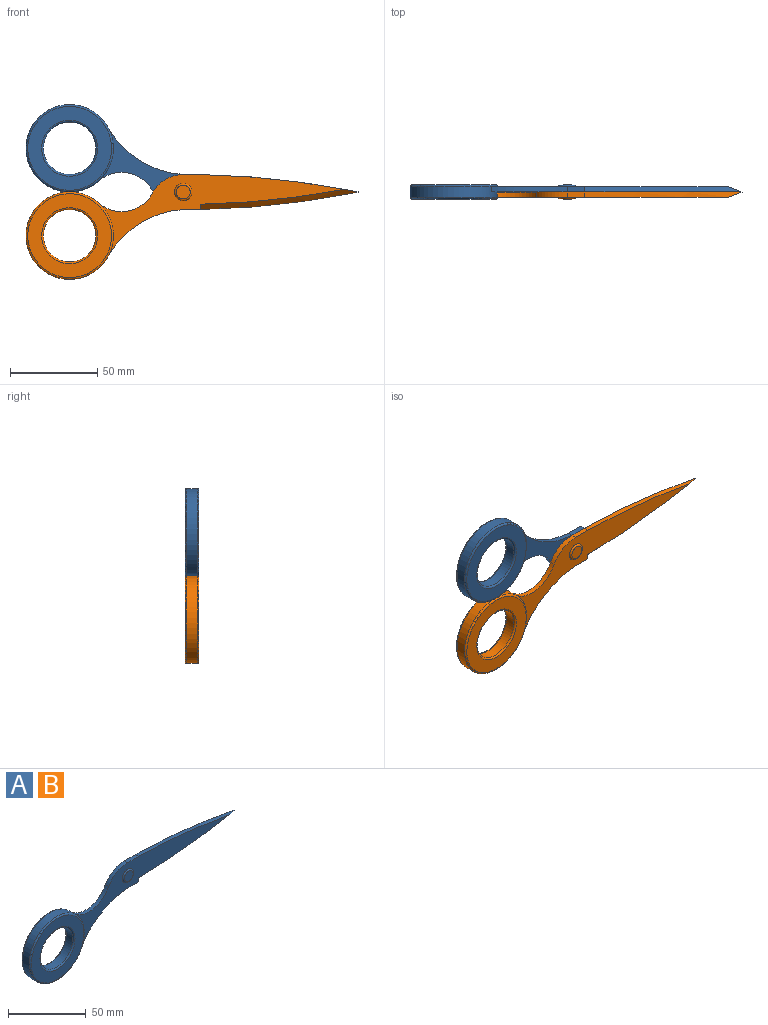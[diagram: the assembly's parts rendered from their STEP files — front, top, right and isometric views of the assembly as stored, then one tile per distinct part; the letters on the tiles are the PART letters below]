
ASSEMBLY  parts=2 mates=1
PART A: 20 faces, bbox 192.1x8x62.1 mm
  f0: plane 140.7x47.21mm, normal (0,-1,0), area 1652.2mm2, adj f2,f3,f4,f5,f7,f8,f13,f14
  f1: plane 148.49x47.21mm, normal (0,1,0), area 1990.9mm2, adj f2,f3,f4,f5,f6,f7,f8,f13
  f2: plane 10x3mm, normal (0,0,1), area 30mm2, adj f0,f1,f4,f8
  f3: plane 10x3mm, normal (0,0,-1), area 30mm2, adj f0,f1,f7,f14
  f4: cylinder r=500mm len=90mm, axis (0,1,0), area 260.3mm2, adj f0,f1,f2,f13
  f5: cylinder r=20mm len=31.17mm, axis (0,1,0), area 110.2mm2, adj f0,f1,f6,f8
  f6: cylinder r=25mm len=50mm, axis (0,1,0), area 840.5mm2, adj f1,f5,f7,f15,f17
  f7: cylinder r=53.39mm len=43.18mm, axis (0,1,0), area 159.6mm2, adj f0,f1,f3,f6
  f8: cylinder r=20mm len=17.32mm, axis (0,1,0), area 62.8mm2, adj f0,f1,f2,f5
  f9: plane 48x48mm, normal (0,1,0), area 1005.3mm2, adj f16,f17
  f10: cylinder r=15mm len=30mm, axis (0,1,0), area 565.5mm2, adj f16,f18
  f11: plane 48x48mm, normal (0,-1,0), area 1005.3mm2, adj f15,f18
  f12: plane 8x8mm, normal (0,-1,0), area 50.3mm2, adj f19
  f13: bspline ~90x12.95mm, area 368.1mm2, adj f0,f1,f4,f14
  f14: plane 3x3mm, normal (1,0,0), area 4.5mm2, adj f0,f3,f13
  f15: torus R=24mm, axis (0,-1,0), area 243.2mm2, adj f0,f6,f11
  f16: torus R=16mm, axis (0,-1,0), area 151.6mm2, adj f9,f10
  f17: torus R=24mm, axis (0,-1,0), area 243.2mm2, adj f6,f9
  f18: torus R=16mm, axis (0,-1,0), area 151.6mm2, adj f10,f11
  f19: torus R=4mm, axis (0,-1,0), area 45.8mm2, adj f0,f12
PART B: same geometry as A
PLACE A rot(axis=(1,0,0),180deg) t=(8.19,-11.45,-8.6)mm
PLACE B t=(8.19,-11.45,-8.6)mm fixed
MATE revolute B.f19 <-> A.f19  axis (0,-1,0) through (8.19,-11.45,-8.6)mm
